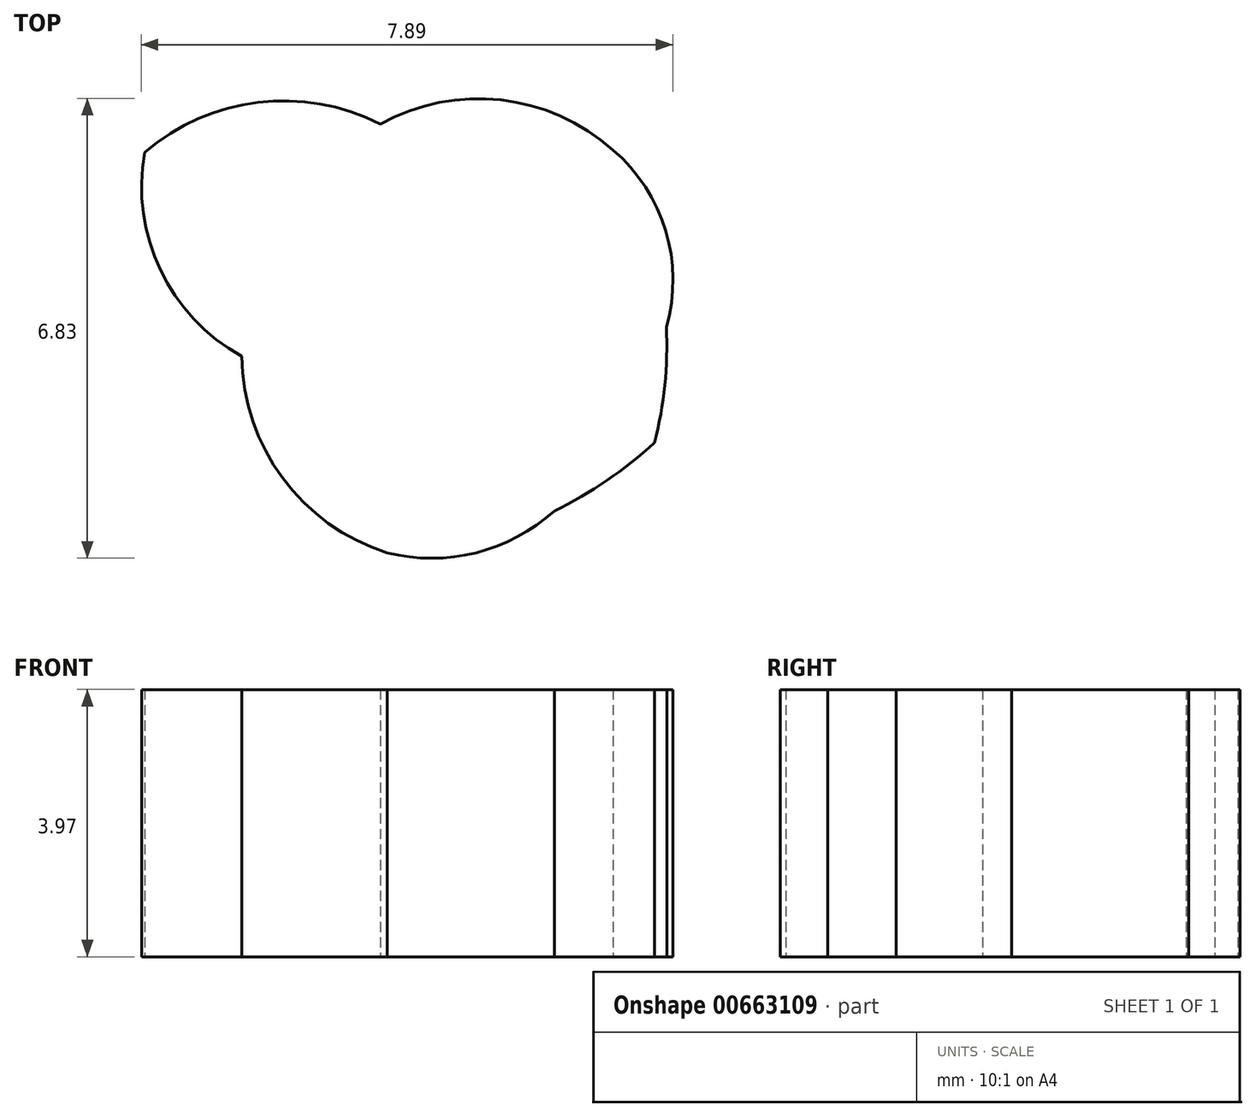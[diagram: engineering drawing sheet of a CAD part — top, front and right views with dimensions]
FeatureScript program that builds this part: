
annotation { "Feature Type Name" : "Feature", "Feature Type Description" : "" }
export const myFeature = defineFeature(function(context is Context, id is Id, definition is map)
    precondition{}
    {
        {
            var Q0;
            Q0=qCreatedBy(makeId("Top.planeOp"),FACE);
            var sketch = newSketch(context, id + "F0", { "sketchPlane" : qUnion([Q0])});
            skPoint(sketch, "E0.center", {"position": v(0, 0) * mm});
            skPoint(sketch, "E1.center", {"position": v(-0.03, 0.1) * mm});
            skLineSegment(sketch, "E2", {"start": v(-12.37, 4.64) * mm, "end": v(-12.37, 4.57) * mm});
            skLineSegment(sketch, "E3", {"start": v(7.76, 1.05) * mm, "end": v(7.76, 1.05) * mm});
            skLineSegment(sketch, "E4", {"start": v(8, -1.42) * mm, "end": v(8, -1.42) * mm});
            skLineSegment(sketch, "E5", {"start": v(6.33, 3.65) * mm, "end": v(6.36, 3.6) * mm});
            skArc(sketch, "E6", {"start": v(2.48, -3.37) * mm, "mid": v(3.26, -2.92) * mm, "end": v(3.97, -2.35) * mm});
            skArc(sketch, "E7", {"start": v(0, -4) * mm, "mid": v(1.32, -3.99) * mm, "end": v(2.48, -3.37) * mm});
            skArc(sketch, "E8", {"start": v(3.97, -2.35) * mm, "mid": v(4.12, -1.5) * mm, "end": v(4.15, -0.64) * mm});
            skArc(sketch, "E9", {"start": v(4.15, -0.64) * mm, "mid": v(4.14, 0.8) * mm, "end": v(3.36, 2) * mm});
            skArc(sketch, "E10", {"start": v(-3.6, 1.96) * mm, "mid": v(-3.37, 0.21) * mm, "end": v(-2.16, -1.07) * mm});
            skArc(sketch, "E11", {"start": v(-2.16, -1.07) * mm, "mid": v(-1.55, -2.88) * mm, "end": v(0, -4) * mm});
            skArc(sketch, "E12", {"start": v(-0.1, 2.38) * mm, "mid": v(-1.92, 2.7) * mm, "end": v(-3.6, 1.96) * mm});
            skArc(sketch, "E13", {"start": v(3.36, 2) * mm, "mid": v(1.69, 2.74) * mm, "end": v(-0.1, 2.38) * mm});
            skSolve(sketch);
        }
        {
            var Q0;
            Q0=makeQuery(id+"F0.imprint","IMPRINT",FACE,{"disambiguationData":[TD([[makeQuery(id+"F0.imprint","IMPRINT",EDGE,{"derivedFrom":sQuery(id+"F0.wireOp",EDGE,"E6")}),1.0]])]});
            extrude(context, id + "F1", {"entities" : qUnion([Q0]), "depth" : 3.97 * mm, "offsetDistance" : 25.4 * mm});
        }
    });
